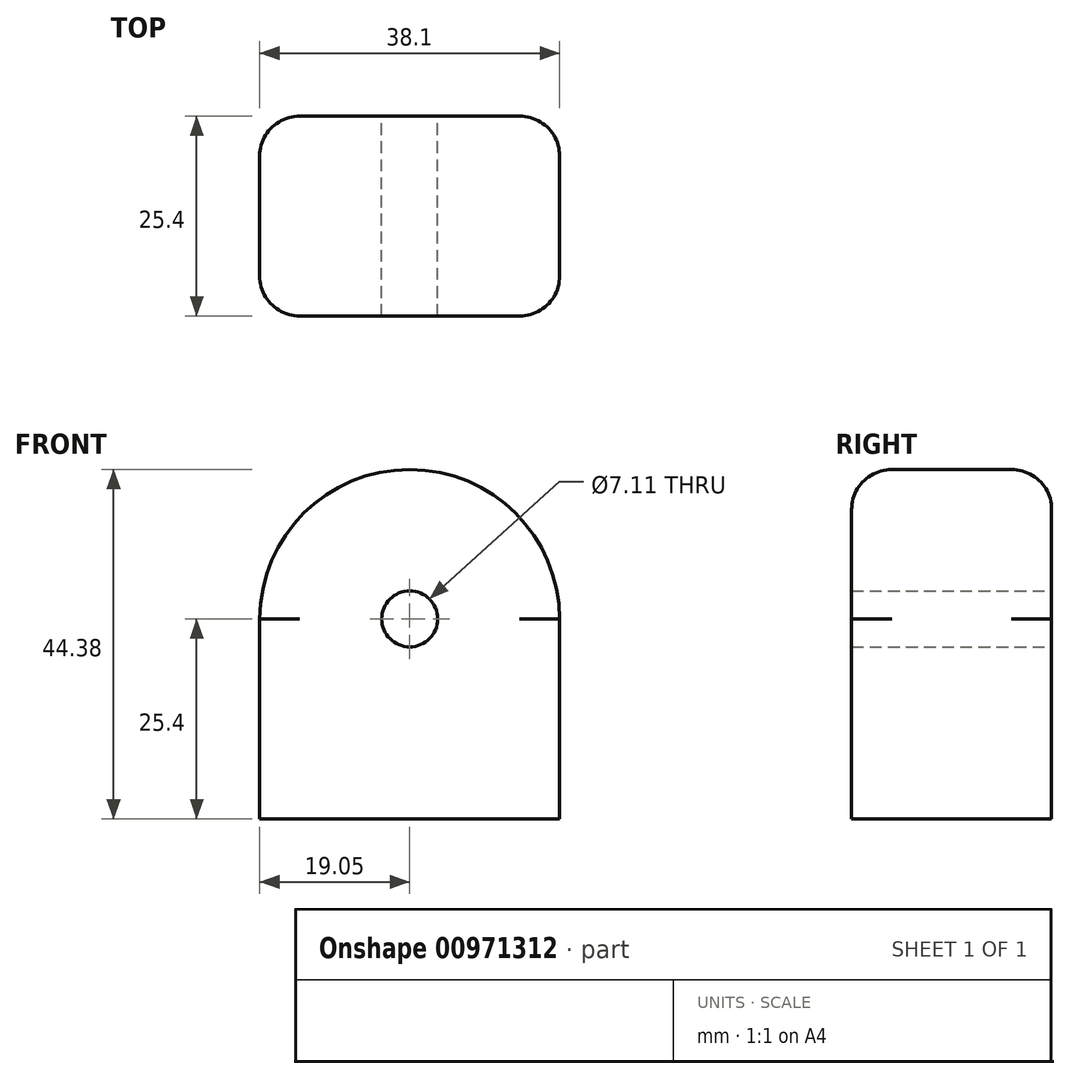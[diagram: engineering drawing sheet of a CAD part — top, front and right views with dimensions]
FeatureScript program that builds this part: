
annotation { "Feature Type Name" : "Feature", "Feature Type Description" : "" }
export const myFeature = defineFeature(function(context is Context, id is Id, definition is map)
    precondition{}
    {
        {
            var Q0;
            Q0=qCreatedBy(makeId("Front.planeOp"),FACE);
            var sketch = newSketch(context, id + "F0", { "sketchPlane" : qUnion([Q0])});
            skLineSegment(sketch, "E0.bottom", {"start": v(19.05, -12.7) * mm, "end": v(-19.05, -12.7) * mm});
            skLineSegment(sketch, "E0.left", {"start": v(19.05, -12.7) * mm, "end": v(19.05, 12.7) * mm});
            skLineSegment(sketch, "E0.right", {"start": v(-19.05, -12.7) * mm, "end": v(-19.05, 12.7) * mm});
            skPoint(sketch, "E0.middle", {"position": v(0, 0) * mm});
            skArc(sketch, "E1", {"start": v(19.05, 12.7) * mm, "mid": v(0, 31.68) * mm, "end": v(-19.05, 12.7) * mm});
            skPoint(sketch, "E2.center.orphan", {"position": v(0, 12.7) * mm});
            skCircle(sketch, "E3", {"center": v(0, 12.7) * mm, "radius": 3.56 * mm});
            skSolve(sketch);
        }
        {
            var Q0;
            Q0=makeQuery(id+"F0.imprint","IMPRINT",FACE,{"disambiguationData":[TD([[makeQuery(id+"F0.imprint","IMPRINT",EDGE,{"derivedFrom":sQuery(id+"F0.wireOp",EDGE,"E0.bottom")}),-1.0]])]});
            extrude(context, id + "F1", {"entities" : qUnion([Q0]), "depth" : 25.4 * mm, "offsetDistance" : 25.4 * mm});
        }
        {
            var Q0;
            Q0 = qSketchRegion(id + "F0", true);
            extrude(context, id + "F2", {"entities" : qUnion([Q0]), "operationType" : NewBodyOperationType.ADD, "depth" : 25.4 * mm, "offsetDistance" : 25.4 * mm});
        }
        {
            var Q0;
            Q0=makeQuery(id+"F1.opExtrude","CAP_EDGE",EDGE,{"disambiguationData":[OSD([sQuery(id+"F0.wireOp",EDGE,"E1")])],"isStart":true});
            var Q1;
            Q1=makeQuery(id+"F1.opExtrude","CAP_EDGE",EDGE,{"disambiguationData":[OSD([sQuery(id+"F0.wireOp",EDGE,"E0.left")])],"isStart":true});
            var Q2;
            Q2=makeQuery(id+"F1.opExtrude","CAP_EDGE",EDGE,{"disambiguationData":[OSD([sQuery(id+"F0.wireOp",EDGE,"E0.right")])],"isStart":true});
            var Q3;
            Q3=makeQuery(id+"F1.opExtrude","CAP_EDGE",EDGE,{"disambiguationData":[OSD([sQuery(id+"F0.wireOp",EDGE,"E1")])],"isStart":false});
            var Q4;
            Q4=makeQuery(id+"F1.opExtrude","CAP_EDGE",EDGE,{"disambiguationData":[OSD([sQuery(id+"F0.wireOp",EDGE,"E0.right")])],"isStart":false});
            var Q5;
            Q5=makeQuery(id+"F1.opExtrude","CAP_EDGE",EDGE,{"disambiguationData":[OSD([sQuery(id+"F0.wireOp",EDGE,"E0.left")])],"isStart":false});
            fillet(context, id + "F3", {"entities" : qUnion([Q0, Q1, Q2, Q3, Q4, Q5]), "radius" : 5.08 * mm, "tangentPropagation" : true, "allowEdgeOverflow" : false});
        }
    });
